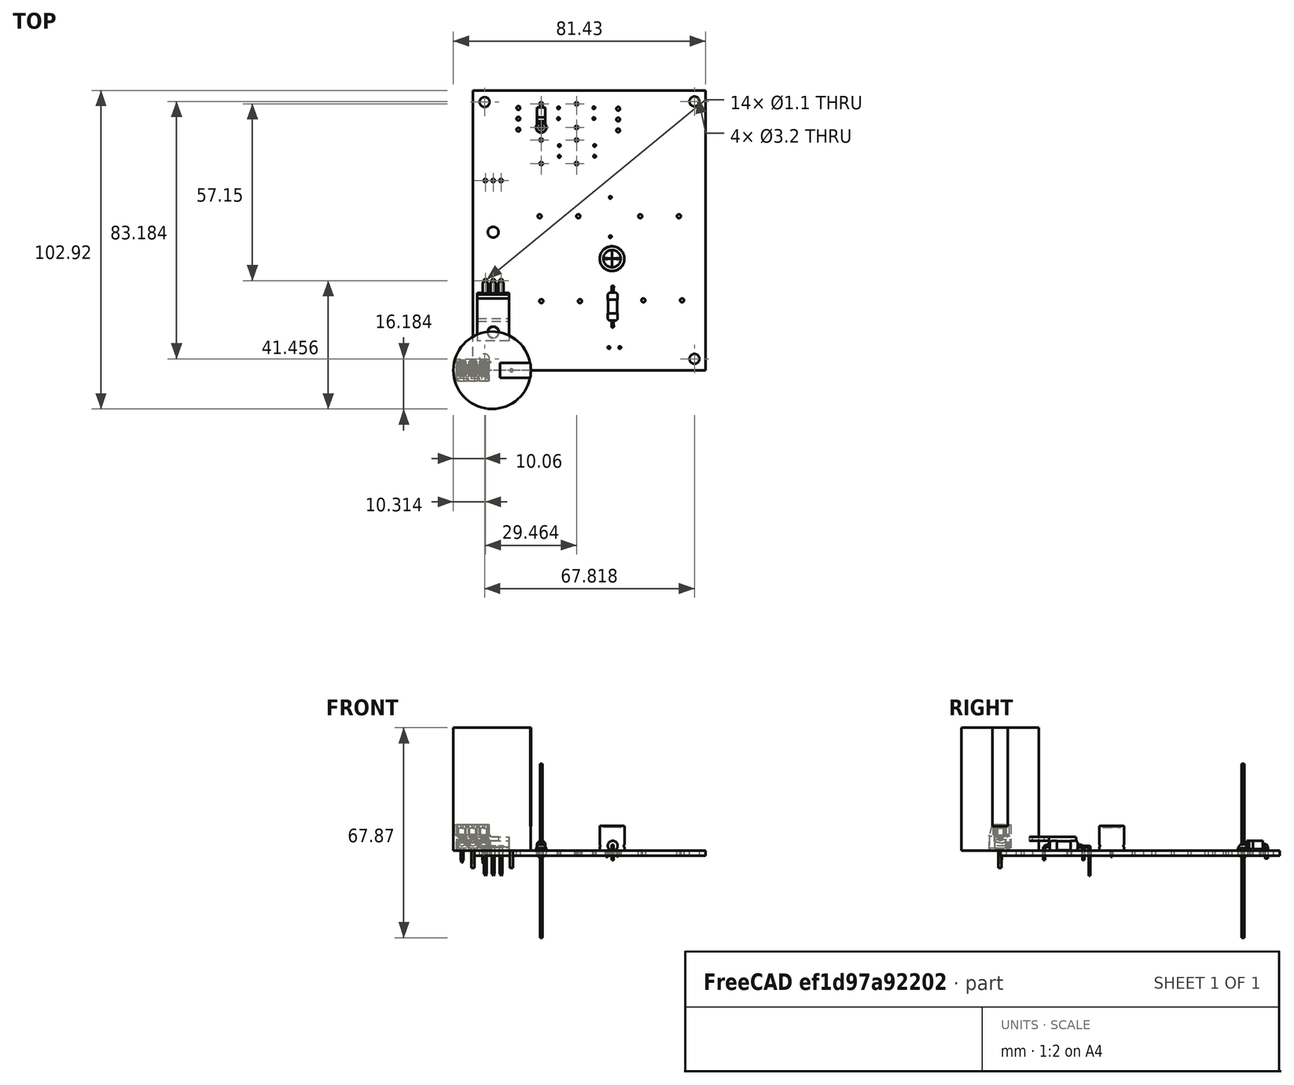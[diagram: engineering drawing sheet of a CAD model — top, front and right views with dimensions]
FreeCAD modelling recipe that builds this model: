
FCSTD DOCUMENT  (FreeCAD 0.19R24267 +148 (Git))
Label: 15v-supply-board
License: All rights reserved
LicenseURL: http://en.wikipedia.org/wiki/All_rights_reserved
objects: Part::Feature×30, App::Link×17, App::Part×7, Sketcher::SketchObject×2, PartDesign::CoordinateSystem×1
note: 33 computed .brp shape members not serialized (recipe doc carries the construction recipe); baked Part::Feature solids carry a one-line shape summary decoded from their .brp

FEATURE [Sketcher::SketchObject] PCB_Sketch_draft
  FullyConstrained = false
  sketch-geometry (4):
    g0: LineSegment StartX=0 StartY=90.424 StartZ=0 EndX=75.184 EndY=90.424 EndZ=0
    g1: LineSegment StartX=75.184 StartY=90.424 StartZ=0 EndX=75.184 EndY=0 EndZ=0
    g2: LineSegment StartX=75.184 StartY=0 StartZ=0 EndX=0 EndY=0 EndZ=0
    g3: LineSegment StartX=0 StartY=0 StartZ=0 EndX=0 EndY=90.424 EndZ=0
  constraints (4):
    c: Coincident(g2,g3)
    c: Coincident(g0,g3)
    c: Coincident(g1,g2)
    c: Coincident(g0,g1)
FEATURE [PartDesign::CoordinateSystem] Local_CS_7b02
  AttacherType = Attacher::AttachEngine3D
FEATURE [Part::Feature] Pcb_7b02
  Placement = pos=(-75.946,138.684,0) rot=(0,0,1;0rad)
  shape: bbox 75.18 x 90.42 x 1.6 mm, 56 faces (baked)
FEATURE [Sketcher::SketchObject] PCB_Sketch_7b02
  FullyConstrained = false
  sketch-geometry (4):
    g0: LineSegment StartX=0 StartY=90.424 StartZ=0 EndX=75.184 EndY=90.424 EndZ=0
    g1: LineSegment StartX=75.184 StartY=90.424 StartZ=0 EndX=75.184 EndY=0 EndZ=0
    g2: LineSegment StartX=75.184 StartY=0 StartZ=0 EndX=0 EndY=0 EndZ=0
    g3: LineSegment StartX=0 StartY=0 StartZ=0 EndX=0 EndY=90.424 EndZ=0
  constraints (4):
    c: Coincident(g2,g3)
    c: Coincident(g0,g3)
    c: Coincident(g1,g2)
    c: Coincident(g0,g1)
FEATURE [Part::Feature] Part__Feature  label="part"
  shape: bbox 0.508 x 0.508 x 4.064 mm, 3 faces (baked)
FEATURE [Part::Feature] Part__Feature001  label="part001"
  shape: bbox 0.508 x 0.508 x 4.064 mm, 3 faces (baked)
FEATURE [Part::Feature] Part__Feature002  label="part002"
  shape: bbox 5.994 x 3.506 x 8.509 mm, 6 faces (baked)
FEATURE [App::Part] part  label="C909_part003_af03f52f8d81"
  Group = -> [Part__Feature,Part__Feature001,Part__Feature002]
  Origin = -> Origin008
  Placement = pos=(39.37,72.644,0) rot=(0,0,-1;1.5708rad)
FEATURE [App::Link] C909_part003_af03f52f8d81_ln_  label="C906_part003_3db3d25175d7"
  LinkPlacement = pos=(27.691,84.808,0) rot=(0,0,-1;1.5708rad)
  LinkedObject = -> part
  Placement = pos=(27.691,84.808,0) rot=(0,0,-1;1.5708rad)
FEATURE [Part::Feature] Part__Feature003  label="SOLID"
  Placement = pos=(0,0,4.2) rot=(0,0,1;0rad)
  shape: bbox 2.75 x 3.75 x 8.15 mm, 17 faces (baked)
FEATURE [Part::Feature] Part__Feature004  label="SOLID001"
  Placement = pos=(0,0,4.2) rot=(0,0,1;0rad)
  shape: bbox 2.75 x 3.75 x 8.15 mm, 17 faces (baked)
FEATURE [Part::Feature] Part__Feature005  label="SOLID002"
  Placement = pos=(0,0,4.2) rot=(0,0,1;0rad)
  shape: bbox 2.75 x 3.75 x 8.15 mm, 17 faces (baked)
FEATURE [Part::Feature] Part__Feature006  label="SOLID003"
  Placement = pos=(0,0,4.2) rot=(0,0,1;0rad)
  shape: bbox 2.9 x 4.5 x 2.65 mm, 46 faces (baked)
FEATURE [Part::Feature] Part__Feature007  label="SOLID004"
  Placement = pos=(0,0,4.2) rot=(0,0,1;0rad)
  shape: bbox 2.9 x 4.5 x 2.65 mm, 46 faces (baked)
FEATURE [Part::Feature] Part__Feature008  label="SOLID005"
  Placement = pos=(0,0,4.2) rot=(0,0,1;0rad)
  shape: bbox 2.9 x 4.5 x 2.65 mm, 46 faces (baked)
FEATURE [Part::Feature] Part__Feature009  label="SOLID006"
  Placement = pos=(0,0,4.2) rot=(0,0,1;0rad)
  shape: bbox 3.139 x 3.139 x 4.6 mm, 17 faces (baked)
FEATURE [Part::Feature] Part__Feature010  label="SOLID007"
  Placement = pos=(0,0,4.2) rot=(0,0,1;0rad)
  shape: bbox 3.139 x 3.139 x 4.6 mm, 17 faces (baked)
FEATURE [Part::Feature] Part__Feature011  label="SOLID008"
  Placement = pos=(0,0,4.2) rot=(0,0,1;0rad)
  shape: bbox 3.139 x 3.139 x 4.6 mm, 17 faces (baked)
FEATURE [Part::Feature] Part__Feature012  label="SOLID009"
  Placement = pos=(0,0,4.2) rot=(0,0,1;0rad)
  shape: bbox 11.5 x 7 x 8.4 mm, 98 faces (baked)
FEATURE [App::Part] _91103110003_1  label="J901_691103110003_1_4d612100a2a6"
  Group = -> [Part__Feature003,Part__Feature004,Part__Feature005,Part__Feature006,Part__Feature007,Part__Feature008,Part__Feature009,Part__Feature010,Part__Feature011,Part__Feature012]
  Origin = -> Origin009
  Placement = pos=(14.732,81.28,0) rot=(0,0,-1;1.5708rad)
FEATURE [App::Link] J901_691103110003_1_4d612100a2a6_ln_  label="J901_691103110003_1_4d612100a2a6[2]"
  LinkPlacement = pos=(14.732,81.28,4) rot=(0,0,-1;1.5708rad)
  LinkedObject = -> _91103110003_1
  Placement = pos=(14.732,81.28,4) rot=(0,0,-1;1.5708rad)
FEATURE [Part::Feature] Shape  label="D901_D_DO-41_SOD81_P7.62mm_Horizontal_0f7420698e15"
  Placement = pos=(22.098,78.486,0) rot=(0,0,1;1.5708rad)
  shape: bbox 2.72 x 8.618 x 5.71 mm, 15 faces (baked)
FEATURE [Part::Feature] Shape001  label="D901_SOD57  BYT62-BY203_6-563-5006-5-4_0f7420698e15[2]"
  Placement = pos=(22.098,78.486,0) rot=(0,0,1;1.5708rad)
  shape: bbox 4.349 x 4.349 x 56.22 mm, 10 faces (baked)
FEATURE [App::Link] D901_D_DO_41_SOD81_P7_62mm_Horizontal_0f7420698e15_ln_  label="D904_D_DO-41_SOD81_P7.62mm_Horizontal_3765f3f7798b"
  LinkPlacement = pos=(33.528,66.802,0) rot=(0,0,1;1.5708rad)
  LinkedObject = -> Shape
  Placement = pos=(33.528,66.802,0) rot=(0,0,1;1.5708rad)
FEATURE [Part::Feature] Part__Feature013  label="part003"
  shape: bbox 1.016 x 1.016 x 5.588 mm, 3 faces (baked)
FEATURE [Part::Feature] Part__Feature014  label="part004"
  shape: bbox 1.016 x 1.016 x 5.588 mm, 3 faces (baked)
FEATURE [Part::Feature] Part__Feature015  label="part005"
  shape: bbox 24.99 x 24.99 x 39.75 mm, 3 faces (baked)
FEATURE [Part::Feature] Part__Feature016  label="part006"
  shape: bbox 10.02 x 4.878 x 31.83 mm, 8 faces (baked)
FEATURE [App::Part] part001  label="C911_part007_10cb9a3285f4"
  Group = -> [Part__Feature013,Part__Feature014,Part__Feature015,Part__Feature016]
  Origin = -> Origin010
  Placement = pos=(54.102,49.784,0) rot=(0,0,1;0rad)
FEATURE [App::Link] C911_part007_10cb9a3285f4_ln_  label="C902_part007_474a571f78e2"
  LinkPlacement = pos=(21.59,49.784,0) rot=(0,0,1;0rad)
  LinkedObject = -> part001
  Placement = pos=(21.59,49.784,0) rot=(0,0,1;0rad)
FEATURE [Part::Feature] Shape002  label="R902_R_Axial_DIN0309_L90mm_D32mm_P1270mm_Horizontal_656395d6a1e4"
  Placement = pos=(45.212,14.224,0) rot=(0,0,1;1.5708rad)
  shape: bbox 3.464 x 13.63 x 6.332 mm, 17 faces (baked)
FEATURE [App::Link] C911_part007_10cb9a3285f4_ln_001  label="C910_part007_5ecea69d9437"
  LinkPlacement = pos=(55.118,22.606,0) rot=(0,0,1;0rad)
  LinkedObject = -> part001
  Placement = pos=(55.118,22.606,0) rot=(0,0,1;0rad)
FEATURE [App::Link] C909_part003_af03f52f8d81_ln_001  label="C907_part007_ae6a843ea56a"
  LinkPlacement = pos=(27.945,72.616,0) rot=(0,0,-1;1.5708rad)
  LinkedObject = -> part
  Placement = pos=(27.945,72.616,0) rot=(0,0,-1;1.5708rad)
FEATURE [Part::Feature] Shape003  label="C904_CP_Radial_D80mm_P350mm_be9362f17a2f"
  Placement = pos=(43.2449,36.068,0) rot=(0,0,1;0rad)
  shape: bbox 9.886 x 10.23 x 10 mm, 54 faces (baked)
FEATURE [App::Link] D901_D_DO_41_SOD81_P7_62mm_Horizontal_0f7420698e15_ln_001  label="D902_D_DO-41_SOD81_P7.62mm_Horizontal_acca8f042afe"
  LinkPlacement = pos=(22.098,66.802,0) rot=(0,0,1;1.5708rad)
  LinkedObject = -> Shape
  Placement = pos=(22.098,66.802,0) rot=(0,0,1;1.5708rad)
FEATURE [App::Link] C904_CP_Radial_D80mm_P350mm_be9362f17a2f_ln_  label="C905_CP_Radial_D80mm_P350mm_1a9500cd5eb0"
  LinkPlacement = pos=(44.0069,7.366,0) rot=(0,0,1;0rad)
  LinkedObject = -> Shape003
  Placement = pos=(44.0069,7.366,0) rot=(0,0,1;0rad)
FEATURE [App::Link] R902_R_Axial_DIN0309_L90mm_D32mm_P1270mm_Horizontal_656395d6a1e4_ln_  label="R901_R_Axial_DIN0309_L90mm_D32mm_P1270mm_Horizontal_c8b94c641cc7"
  LinkPlacement = pos=(44.45,43.18,0) rot=(0,0,1;1.5708rad)
  LinkedObject = -> Shape002
  Placement = pos=(44.45,43.18,0) rot=(0,0,1;1.5708rad)
FEATURE [Part::Feature] Shape004  label="U902_TO-220-3_Horizontal_TabUp_336c31f2f8c4"
  Placement = pos=(4.064,28.956,0) rot=(0,0,1;0rad)
  shape: bbox 10.25 x 19.74 x 12.59 mm, 80 faces (baked)
FEATURE [App::Link] U902_TO_220_3_Horizontal_TabUp_336c31f2f8c4_ln_  label="U902_TO-220-3_Horizontal_TabUp_336c31f2f8c4[2]"
  LinkPlacement = pos=(4.064,28.956,0) rot=(0,0,1;0rad)
  LinkedObject = -> Shape004
  Placement = pos=(4.064,28.956,0) rot=(0,0,1;0rad)
FEATURE [App::Link] J901_691103110003_1_4d612100a2a6_ln_001  label="J902_691103110003_1_2f685726ded9"
  LinkPlacement = pos=(46.99,81.026,0) rot=(0,0,1;1.5708rad)
  LinkedObject = -> _91103110003_1
  Placement = pos=(46.99,81.026,0) rot=(0,0,1;1.5708rad)
FEATURE [App::Link] J901_691103110003_1_4d612100a2a6_ln_002  label="J902_691103110003_1_2f685726ded9[2]"
  LinkPlacement = pos=(46.99,81.026,4) rot=(0,0,1;1.5708rad)
  LinkedObject = -> _91103110003_1
  Placement = pos=(46.99,81.026,4) rot=(0,0,1;1.5708rad)
FEATURE [App::Link] D901_D_DO_41_SOD81_P7_62mm_Horizontal_0f7420698e15_ln_002  label="D903_D_DO-41_SOD81_P7.62mm_Horizontal_fd54faef2eec"
  LinkPlacement = pos=(33.528,78.486,0) rot=(0,0,1;1.5708rad)
  LinkedObject = -> Shape
  Placement = pos=(33.528,78.486,0) rot=(0,0,1;1.5708rad)
FEATURE [App::Link] U902_TO_220_3_Horizontal_TabUp_336c31f2f8c4_ln_001  label="U901_TO-220-3_Horizontal_TabUp_2bf8607644b3"
  LinkPlacement = pos=(4.064,61.3,0) rot=(0,0,1;0rad)
  LinkedObject = -> Shape004
  Placement = pos=(4.064,61.3,0) rot=(0,0,1;0rad)
FEATURE [App::Link] U902_TO_220_3_Horizontal_TabUp_336c31f2f8c4_ln_002  label="U901_TO-220-3_Horizontal_TabUp_2bf8607644b3[2]"
  LinkPlacement = pos=(4.064,61.3,0) rot=(0,0,1;0rad)
  LinkedObject = -> Shape004
  Placement = pos=(4.064,61.3,0) rot=(0,0,1;0rad)
FEATURE [App::Link] C909_part003_af03f52f8d81_ln_002  label="C908_part007_641f8a291a63"
  LinkPlacement = pos=(39.121,84.836,0) rot=(0,0,-1;1.5708rad)
  LinkedObject = -> part
  Placement = pos=(39.121,84.836,0) rot=(0,0,-1;1.5708rad)
FEATURE [App::Link] C911_part007_10cb9a3285f4_ln_002  label="C903_part007_61d36386d3d2"
  LinkPlacement = pos=(22.1411,22.352,0) rot=(0,0,1;0rad)
  LinkedObject = -> part001
  Placement = pos=(22.1411,22.352,0) rot=(0,0,1;0rad)
FEATURE [App::Part] Top_7b02
  Group = -> [part,C909_part003_af03f52f8d81_ln_,_91103110003_1,J901_691103110003_1_4d612100a2a6_ln_,Shape,Shape001,D901_D_DO_41_SOD81_P7_62mm_Horizontal_0f7420698e15_ln_,part001,C911_part007_10cb9a3285f4_ln_,Shape002,C911_part007_10cb9a3285f4_ln_001,C909_part003_af03f52f8d81_ln_001,Shape003,D901_D_DO_41_SOD81_P7_62mm_Horizontal_0f7420698e15_ln_001,C904_CP_Radial_D80mm_P350mm_be9362f17a2f_ln_,+10 more]
  Origin = -> Origin003
FEATURE [App::Part] Step_Models_7b02
  Group = -> [Top_7b02]
  Origin = -> Origin002
FEATURE [Part::Feature] pads_area024001  label="topPads_7b02"
  Placement = pos=(-75.946,138.684,0.02) rot=(0,0,1;0rad)
  shape: bbox 65.39 x 80.64 x 2e-07 mm, 44 faces, 0 solids (baked)
FEATURE [Part::Feature] tracks_area001  label="topTracks_7b02"
  Placement = pos=(-75.946,138.684,0.01) rot=(0,0,1;0rad)
  shape: bbox 44.87 x 78.49 x 2e-07 mm, 14 faces, 0 solids (baked)
FEATURE [Part::Feature] zones_area001  label="topZones_7b02"
  Placement = pos=(-75.946,138.684,0.01) rot=(0,0,1;0rad)
  shape: bbox 74.42 x 89.66 x 2e-07 mm, 1 faces, 0 solids (baked)
FEATURE [Part::Feature] pads_area024026001  label="botPads_7b02"
  Placement = pos=(-75.946,138.684,-1.62) rot=(0,0,1;0rad)
  shape: bbox 65.39 x 80.64 x 2e-07 mm, 44 faces, 0 solids (baked)
FEATURE [Part::Feature] tracks_area002001  label="botTracks_7b02"
  Placement = pos=(-75.946,138.684,-1.61) rot=(0,0,1;0rad)
  shape: bbox 62.91 x 78.49 x 2e-07 mm, 17 faces, 0 solids (baked)
FEATURE [Part::Feature] zones_area002001  label="botZones_7b02"
  Placement = pos=(-75.946,138.684,-1.61) rot=(0,0,1;0rad)
  shape: bbox 74.42 x 89.66 x 2e-07 mm, 1 faces, 0 solids (baked)
FEATURE [Part::Feature] topSilks_5a83
  Placement = pos=(-75.946,138.684,0.07) rot=(0,0,1;0rad)
  shape: bbox 72.69 x 86.78 x 2e-07 mm, 264 faces, 0 solids (baked)
FEATURE [App::Part] Board_Geoms_7b02
  Group = -> [Local_CS_7b02,Pcb_7b02,PCB_Sketch_7b02,pads_area024001,tracks_area001,zones_area001,pads_area024026001,tracks_area002001,zones_area002001,topSilks_5a83]
  Origin = -> Origin
FEATURE [App::Part] Board_7b02  label="15v-supply"
  Group = -> [Board_Geoms_7b02,Step_Models_7b02]
  Origin = -> Origin001
